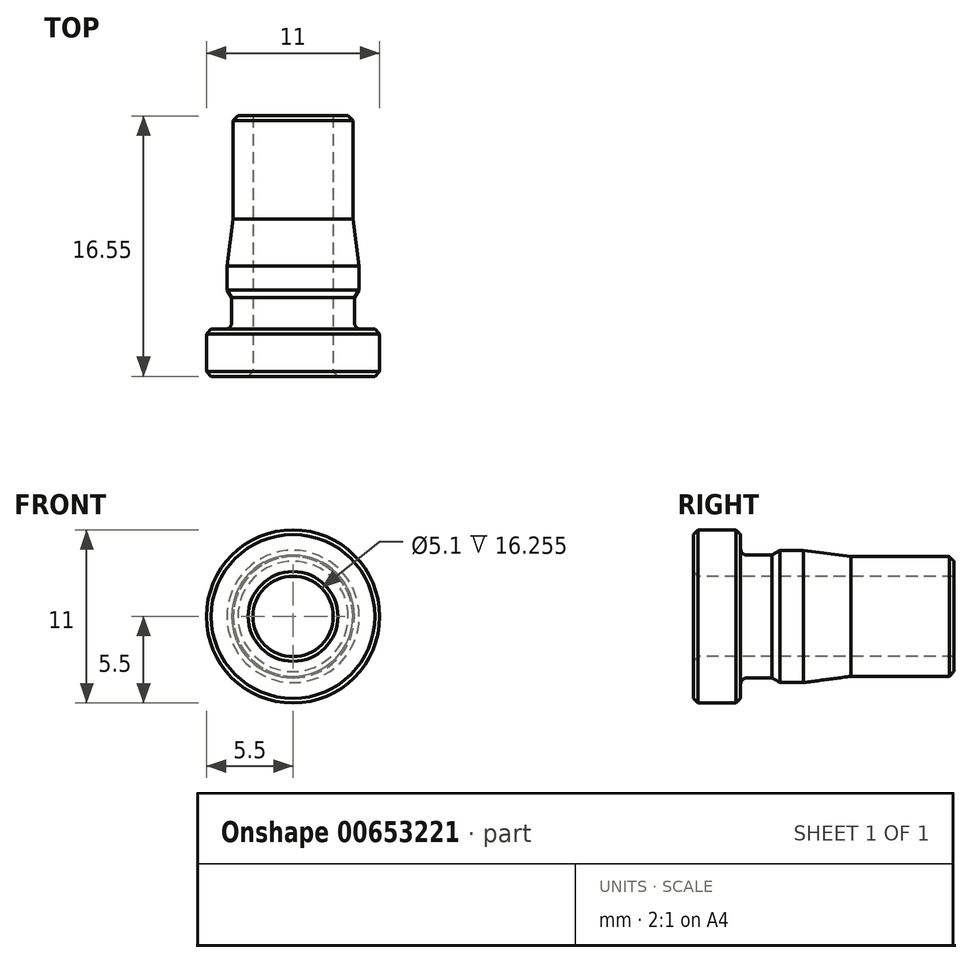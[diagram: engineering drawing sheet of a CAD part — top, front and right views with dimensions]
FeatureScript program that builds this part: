
annotation { "Feature Type Name" : "Feature", "Feature Type Description" : "" }
export const myFeature = defineFeature(function(context is Context, id is Id, definition is map)
    precondition{}
    {
        {
            var Q0;
            Q0=qCreatedBy(makeId("Right.planeOp"),FACE);
            var sketch = newSketch(context, id + "F0", { "sketchPlane" : qUnion([Q0])});
            skLineSegment(sketch, "E0", {"start": v(0, 2.55) * mm, "end": v(0, 5.5) * mm});
            skLineSegment(sketch, "E1", {"start": v(0, 5.5) * mm, "end": v(3, 5.5) * mm});
            skLineSegment(sketch, "E2", {"start": v(3, 5.5) * mm, "end": v(3, 3.9) * mm});
            skLineSegment(sketch, "E3", {"start": v(3, 3.9) * mm, "end": v(5, 3.9) * mm});
            skLineSegment(sketch, "E4", {"start": v(5, 3.9) * mm, "end": v(5.5, 4.2) * mm});
            skLineSegment(sketch, "E5", {"start": v(10, 3.8) * mm, "end": v(16.55, 3.8) * mm});
            skLineSegment(sketch, "E6", {"start": v(16.55, 3.8) * mm, "end": v(16.55, 2.55) * mm});
            skLineSegment(sketch, "E7", {"start": v(0, 2.55) * mm, "end": v(16.55, 2.55) * mm});
            skLineSegment(sketch, "E8", {"start": v(-1.73, 0) * mm, "end": v(21.15, 0) * mm});
            skLineSegment(sketch, "E9", {"start": v(5.5, 4.2) * mm, "end": v(7, 4.2) * mm});
            skLineSegment(sketch, "E10", {"start": v(7, 4.2) * mm, "end": v(10, 3.8) * mm});
            skSolve(sketch);
        }
        {
            var Q0;
            Q0=makeQuery(id+"F0.imprint","IMPRINT",FACE,{"disambiguationData":[TD([[makeQuery(id+"F0.imprint","IMPRINT",EDGE,{"derivedFrom":sQuery(id+"F0.wireOp",EDGE,"E0")}),-1.0]])]});
            var Q1;
            Q1=sQuery(id+"F0.wireOp",EDGE,"E8");
            revolve(context, id + "F1", {"entities" : qUnion([Q0]), "axis" : qUnion([Q1]), "revolveType" : RevolveType.FULL});
        }
        {
            var Q0;
            Q0=makeQuery(id+"F1.opRevolve","SWEPT_EDGE",EDGE,{"disambiguationData":[OSD([sQuery(id+"F0.wireOp",EDGE,"E2"),sQuery(id+"F0.wireOp",EDGE,"E3")])]});
            fillet(context, id + "F2", {"entities" : qUnion([Q0]), "radius" : .4 * mm, "tangentPropagation" : true, "allowEdgeOverflow" : false});
        }
        {
            var Q0;
            Q0=makeQuery(id+"F1.opRevolve","SWEPT_EDGE",EDGE,{"disambiguationData":[OSD([sQuery(id+"F0.wireOp",EDGE,"E1"),sQuery(id+"F0.wireOp",EDGE,"E2")])]});
            var Q1;
            Q1=makeQuery(id+"F1.opRevolve","SWEPT_EDGE",EDGE,{"disambiguationData":[OSD([sQuery(id+"F0.wireOp",EDGE,"E0"),sQuery(id+"F0.wireOp",EDGE,"E1")])]});
            var Q2;
            Q2=makeQuery(id+"F1.opRevolve","SWEPT_EDGE",EDGE,{"disambiguationData":[OSD([sQuery(id+"F0.wireOp",EDGE,"E5"),sQuery(id+"F0.wireOp",EDGE,"E6")])]});
            var Q3;
            Q3=makeQuery(id+"F1.opRevolve","SWEPT_EDGE",EDGE,{"disambiguationData":[OSD([sQuery(id+"F0.wireOp",EDGE,"E0"),sQuery(id+"F0.wireOp",EDGE,"E7")])]});
            chamfer(context, id + "F3", {"entities" : qUnion([Q0, Q1, Q2, Q3]), "width" : .3 * mm, "tangentPropagation" : true});
        }
    });
